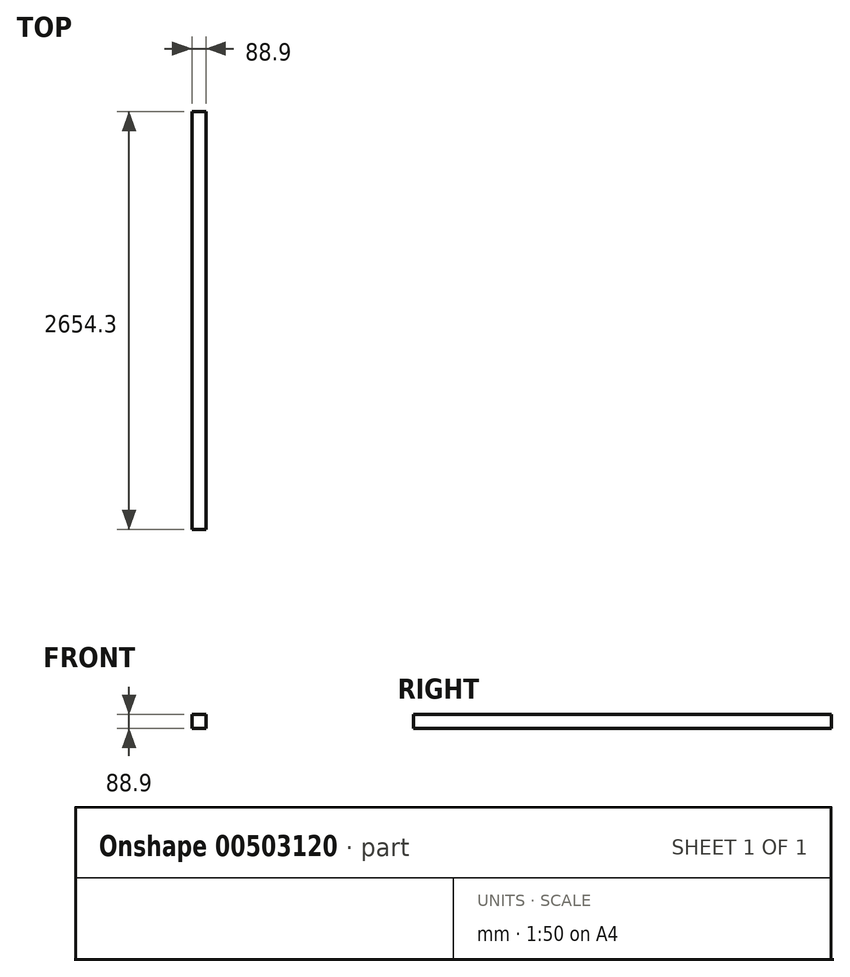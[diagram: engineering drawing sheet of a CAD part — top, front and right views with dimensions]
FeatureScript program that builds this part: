
annotation { "Feature Type Name" : "Feature", "Feature Type Description" : "" }
export const myFeature = defineFeature(function(context is Context, id is Id, definition is map)
    precondition{}
    {
        {
            var Q0;
            Q0=qCreatedBy(makeId("Front.planeOp"),FACE);
            var sketch = newSketch(context, id + "F0", { "sketchPlane" : qUnion([Q0])});
            skLineSegment(sketch, "E0.bottom", {"start": v(0, 0) * mm, "end": v(88.9, 0) * mm});
            skLineSegment(sketch, "E0.top", {"start": v(0, 88.9) * mm, "end": v(88.9, 88.9) * mm});
            skLineSegment(sketch, "E0.left", {"start": v(0, 0) * mm, "end": v(0, 88.9) * mm});
            skLineSegment(sketch, "E0.right", {"start": v(88.9, 0) * mm, "end": v(88.9, 88.9) * mm});
            skSolve(sketch);
        }
        {
            var Q0;
            Q0 = qSketchRegion(id + "F0", true);
            extrude(context, id + "F1", {"entities" : qUnion([Q0]), "depth" : 2654.3 * mm});
        }
    });
